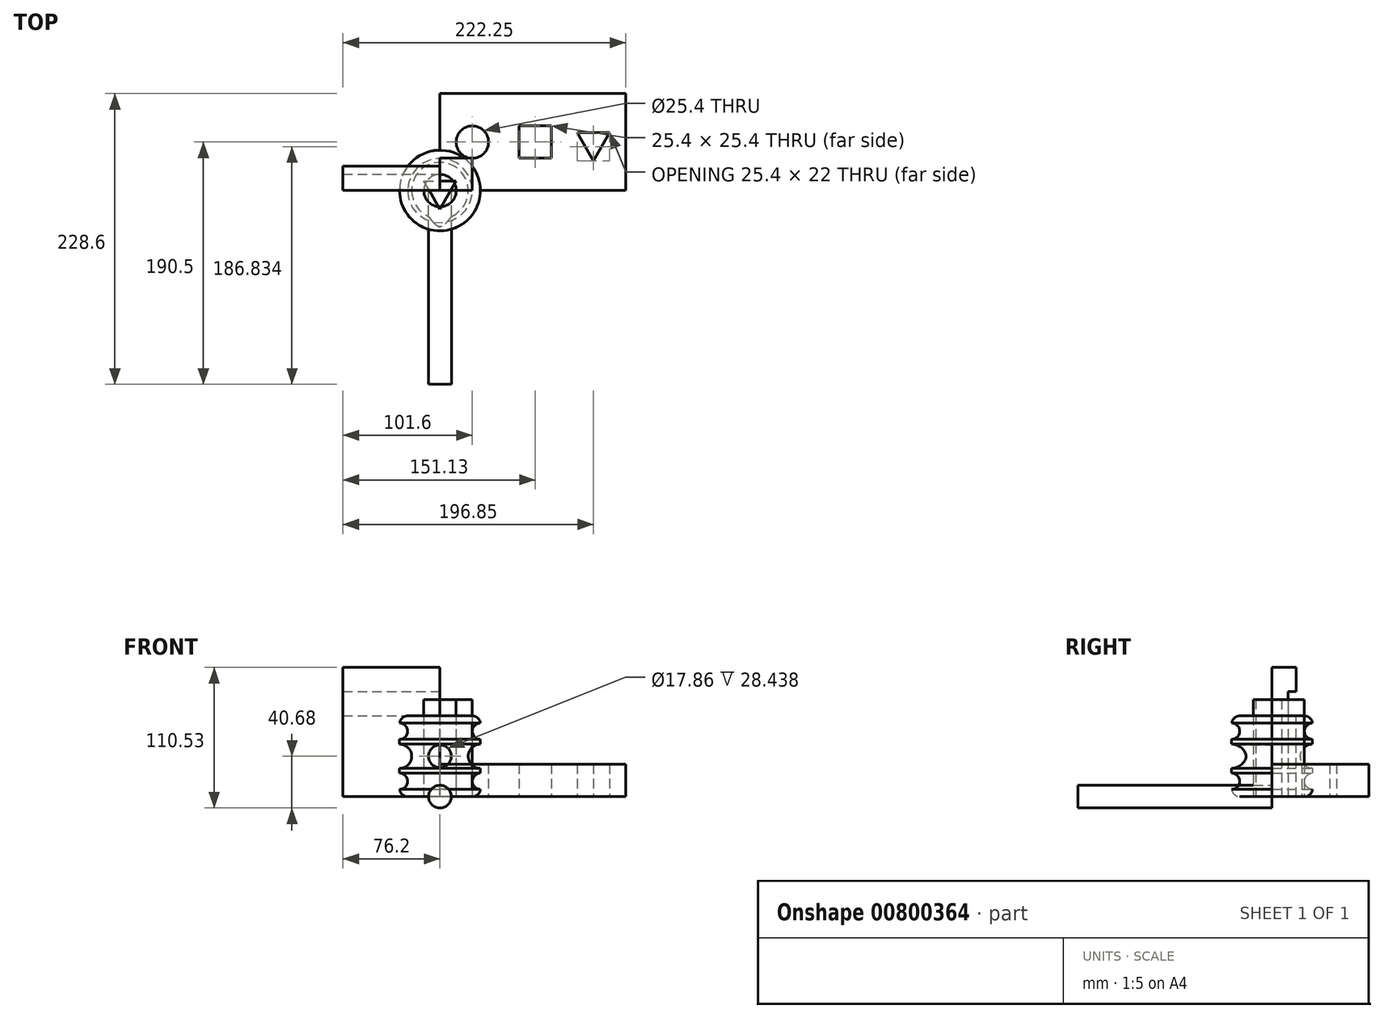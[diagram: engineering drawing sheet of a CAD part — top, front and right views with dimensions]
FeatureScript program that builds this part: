
annotation { "Feature Type Name" : "Feature", "Feature Type Description" : "" }
export const myFeature = defineFeature(function(context is Context, id is Id, definition is map)
    precondition{}
    {
        {
            var Q0;
            Q0=qCreatedBy(makeId("Top.planeOp"),FACE);
            var sketch = newSketch(context, id + "F0", { "sketchPlane" : qUnion([Q0])});
            skCircle(sketch, "E0", {"center": v(0, 0) * mm, "radius": 12.7 * mm});
            skSolve(sketch);
        }
        {
            var Q0;
            Q0 = qSketchRegion(id + "F0", true);
            extrude(context, id + "F1", {"entities" : qUnion([Q0]), "depth" : 76.2 * mm, "offsetDistance" : 25.4 * mm});
        }
        {
            var Q0;
            Q0=qCreatedBy(makeId("Top.planeOp"),FACE);
            var sketch = newSketch(context, id + "F2", { "sketchPlane" : qUnion([Q0])});
            skLineSegment(sketch, "E1.bottom", {"start": v(0, 0) * mm, "end": v(25.4, 0) * mm});
            skLineSegment(sketch, "E1.top", {"start": v(0, 25.4) * mm, "end": v(25.4, 25.4) * mm});
            skLineSegment(sketch, "E1.left", {"start": v(0, 0) * mm, "end": v(0, 25.4) * mm});
            skLineSegment(sketch, "E1.right", {"start": v(25.4, 0) * mm, "end": v(25.4, 25.4) * mm});
            skSolve(sketch);
        }
        {
            var Q0;
            Q0 = qSketchRegion(id + "F2", true);
            extrude(context, id + "F3", {"entities" : qUnion([Q0]), "depth" : 76.2 * mm, "offsetDistance" : 25.4 * mm});
        }
        {
            var Q0;
            Q0=qCreatedBy(makeId("Top.planeOp"),FACE);
            var sketch = newSketch(context, id + "F4", { "sketchPlane" : qUnion([Q0])});
            skCircle(sketch, "E2.cCircle", {"center": v(0, 0) * mm, "radius": 7.33 * mm, "construction": true});
            skLineSegment(sketch, "E2.0", {"start": v(-12.7, 7.33) * mm, "end": v(12.7, 7.33) * mm});
            skLineSegment(sketch, "E2.1", {"start": v(12.7, 7.33) * mm, "end": v(0, -14.66) * mm});
            skLineSegment(sketch, "E2.2", {"start": v(0, -14.66) * mm, "end": v(-12.7, 7.33) * mm});
            skPoint(sketch, "E2.0.midPoint", {"position": v(0, 7.33) * mm});
            skSolve(sketch);
        }
        {
            var Q0;
            Q0 = qSketchRegion(id + "F4", true);
            extrude(context, id + "F5", {"entities" : qUnion([Q0]), "depth" : 76.2 * mm, "offsetDistance" : 25.4 * mm});
        }
        {
            var Q0;
            Q0=qCreatedBy(makeId("Top.planeOp"),FACE);
            var sketch = newSketch(context, id + "F6", { "sketchPlane" : qUnion([Q0])});
            skLineSegment(sketch, "E3.bottom", {"start": v(0, 0) * mm, "end": v(146.05, 0) * mm});
            skLineSegment(sketch, "E3.top", {"start": v(0, 76.2) * mm, "end": v(146.05, 76.2) * mm});
            skLineSegment(sketch, "E3.left", {"start": v(0, 0) * mm, "end": v(0, 76.2) * mm});
            skLineSegment(sketch, "E3.right", {"start": v(146.05, 0) * mm, "end": v(146.05, 76.2) * mm});
            skCircle(sketch, "E4", {"center": v(25.4, 38.1) * mm, "radius": 12.7 * mm});
            skPoint(sketch, "E4.centerSnap0", {"position": v(146.05, 38.1) * mm});
            skLineSegment(sketch, "E5.bottom", {"start": v(62.23, 50.8) * mm, "end": v(87.63, 50.8) * mm});
            skLineSegment(sketch, "E5.top", {"start": v(62.23, 25.4) * mm, "end": v(87.63, 25.4) * mm});
            skLineSegment(sketch, "E5.left", {"start": v(62.23, 50.8) * mm, "end": v(62.23, 25.4) * mm});
            skLineSegment(sketch, "E5.right", {"start": v(87.63, 50.8) * mm, "end": v(87.63, 25.4) * mm});
            skCircle(sketch, "E6.cCircle", {"center": v(120.65, 38.1) * mm, "radius": 7.33 * mm, "construction": true});
            skLineSegment(sketch, "E6.0", {"start": v(107.95, 45.43) * mm, "end": v(133.35, 45.43) * mm});
            skLineSegment(sketch, "E6.1", {"start": v(133.35, 45.43) * mm, "end": v(120.65, 23.44) * mm});
            skLineSegment(sketch, "E6.2", {"start": v(120.65, 23.44) * mm, "end": v(107.95, 45.43) * mm});
            skPoint(sketch, "E6.0.midPoint", {"position": v(120.65, 45.43) * mm});
            skSolve(sketch);
        }
        {
            var Q0;
            Q0=makeQuery(id+"F6.imprint","IMPRINT",FACE,{"disambiguationData":[TD([[makeQuery(id+"F6.imprint","IMPRINT",EDGE,{"derivedFrom":sQuery(id+"F6.wireOp",EDGE,"E3.bottom")}),1.0]])]});
            extrude(context, id + "F7", {"entities" : qUnion([Q0]), "depth" : 25.4 * mm, "offsetDistance" : 25.4 * mm});
        }
        {
            var Q0;
            Q0=qCreatedBy(makeId("Right.planeOp"),FACE);
            var sketch = newSketch(context, id + "F8", { "sketchPlane" : qUnion([Q0])});
            skLineSegment(sketch, "E7.bottom", {"start": v(0, 0) * mm, "end": v(19.05, 0) * mm});
            skLineSegment(sketch, "E7.top", {"start": v(0, 101.6) * mm, "end": v(19.05, 101.6) * mm});
            skLineSegment(sketch, "E7.left", {"start": v(0, 0) * mm, "end": v(0, 101.6) * mm});
            skLineSegment(sketch, "E7.right", {"start": v(19.05, 0) * mm, "end": v(19.05, 101.6) * mm});
            skLineSegment(sketch, "E8.bottom", {"start": v(19.05, 82.55) * mm, "end": v(12.7, 82.55) * mm});
            skLineSegment(sketch, "E8.top", {"start": v(19.05, 63.5) * mm, "end": v(12.7, 63.5) * mm});
            skLineSegment(sketch, "E8.left", {"start": v(19.05, 82.55) * mm, "end": v(19.05, 63.5) * mm});
            skLineSegment(sketch, "E8.right", {"start": v(12.7, 82.55) * mm, "end": v(12.7, 63.5) * mm});
            skSolve(sketch);
        }
        {
            var Q0;
            {var subQ1=sQuery(id+"F8.wireOp",EDGE,"E7.bottom");Q0=makeQuery(id+"F8.imprint","IMPRINT",FACE,{"disambiguationData":[TD([[makeQuery(id+"F8.imprint","IMPRINT",EDGE,{"derivedFrom":subQ1}),1.0]])]});}
            extrude(context, id + "F9", {"entities" : qUnion([Q0]), "oppositeDirection" : true, "depth" : 76.2 * mm, "offsetDistance" : 25.4 * mm});
        }
        {
            var Q0;
            Q0=qCreatedBy(makeId("Front.planeOp"),FACE);
            var sketch = newSketch(context, id + "F10", { "sketchPlane" : qUnion([Q0])});
            skLineSegment(sketch, "E9.bottom", {"start": v(0, 0) * mm, "end": v(25.4, 0) * mm});
            skLineSegment(sketch, "E9.top", {"start": v(0, 63.5) * mm, "end": v(25.4, 63.5) * mm});
            skLineSegment(sketch, "E9.left", {"start": v(0, 0) * mm, "end": v(0, 63.5) * mm});
            skLineSegment(sketch, "E9.right", {"start": v(31.75, 6.35) * mm, "end": v(31.75, 57.15) * mm});
            skCircle(sketch, "E10", {"center": v(31.75, 31.75) * mm, "radius": 9.53 * mm});
            skCircle(sketch, "E11", {"center": v(31.75, 51.44) * mm, "radius": 6.35 * mm});
            skCircle(sketch, "E12", {"center": v(31.75, 12.07) * mm, "radius": 6.35 * mm});
            skPoint(sketch, "E13.visualSharp", {"position": v(31.75, 63.5) * mm});
            skArc(sketch, "E13.filletArc", {"start": v(31.75, 57.15) * mm, "mid": v(29.9, 61.64) * mm, "end": v(25.4, 63.5) * mm});
            skPoint(sketch, "E14.visualSharp", {"position": v(31.75, 0) * mm});
            skArc(sketch, "E14.filletArc", {"start": v(25.4, 0) * mm, "mid": v(29.9, 1.86) * mm, "end": v(31.75, 6.35) * mm});
            skSolve(sketch);
        }
        {
            var Q0;
            {var subQ11=sQuery(id+"F10.wireOp",EDGE,"E9.bottom");Q0=makeQuery(id+"F10.imprint","IMPRINT",FACE,{"disambiguationData":[TD([[makeQuery(id+"F10.imprint","IMPRINT",EDGE,{"derivedFrom":subQ11}),1.0]])]});}
            var Q1;
            Q1=sQuery(id+"F10.wireOp",EDGE,"E9.left");
            revolve(context, id + "F11", {"surfaceOperationType" : NewSurfaceOperationType.NEW, "entities" : qUnion([Q0]), "axis" : qUnion([Q1]), "revolveType" : RevolveType.FULL});
        }
        {
            var Q0;
            Q0=qCreatedBy(makeId("Front.planeOp"),FACE);
            var sketch = newSketch(context, id + "F12", { "sketchPlane" : qUnion([Q0])});
            skPoint(sketch, "E15", {"position": v(0, 31.75) * mm});
            skSolve(sketch);
        }
        {
            var Q0;
            Q0=sQuery(id+"F12.wireOp",VERTEX,"E15");
            var Q1;
            Q1=makeQuery(id+"F11.opRevolve","SWEPT_BODY",BODY,{"disambiguationData":[OSD([sQuery(id+"F10.wireOp",EDGE,"E9.bottom"),sQuery(id+"F10.wireOp",EDGE,"E9.top"),sQuery(id+"F10.wireOp",EDGE,"E9.left"),sQuery(id+"F10.wireOp",EDGE,"E9.right"),sQuery(id+"F10.wireOp",EDGE,"E10"),sQuery(id+"F10.wireOp",EDGE,"E11"),sQuery(id+"F10.wireOp",EDGE,"E12"),sQuery(id+"F10.wireOp",EDGE,"E13.filletArc"),sQuery(id+"F10.wireOp",EDGE,"E14.filletArc")])]});
            hole(context, id + "F13", {"style" : HoleStyle.SIMPLE, "endStyle" : HoleEndStyle.THROUGH, "oppositeDirection" : true, "standardTappedOrClearance" : lookupTablePath({ "standard" : "ANSI", "engagement" : "75%", "pitch" : "20 tpi", "size" : "3/4", "type" : "Tapped" }), "standardBlindInLast" : lookupTablePath({ "standard" : "ANSI", "engagement" : "75%", "pitch" : "20 tpi", "size" : "3/4", "type" : "Tapped" }), "holeDiameter" : 17.86 * mm, "majorDiameter" : 19.05 * mm, "showTappedDepth" : true, "isTappedThrough" : true, "tappedDepth" : 12.7 * mm, "tapClearance" : 3, "locations" : qUnion([Q0]), "scope" : qUnion([Q1])});
        }
        {
            var Q0;
            Q0=qCreatedBy(makeId("Front.planeOp"),FACE);
            var sketch = newSketch(context, id + "F14", { "sketchPlane" : qUnion([Q0])});
            skCircle(sketch, "E16", {"center": v(0, 0) * mm, "radius": 8.93 * mm});
            skSolve(sketch);
        }
        {
            var Q0;
            Q0=makeQuery(id+"F14.imprint","IMPRINT",FACE,{"disambiguationData":[TD([[makeQuery(id+"F14.imprint","IMPRINT",EDGE,{"derivedFrom":sQuery(id+"F14.wireOp",EDGE,"E16")}),1.0]])]});
            extrude(context, id + "F15", {"entities" : qUnion([Q0]), "depth" : 152.4 * mm, "offsetDistance" : 25.4 * mm});
        }
    });
